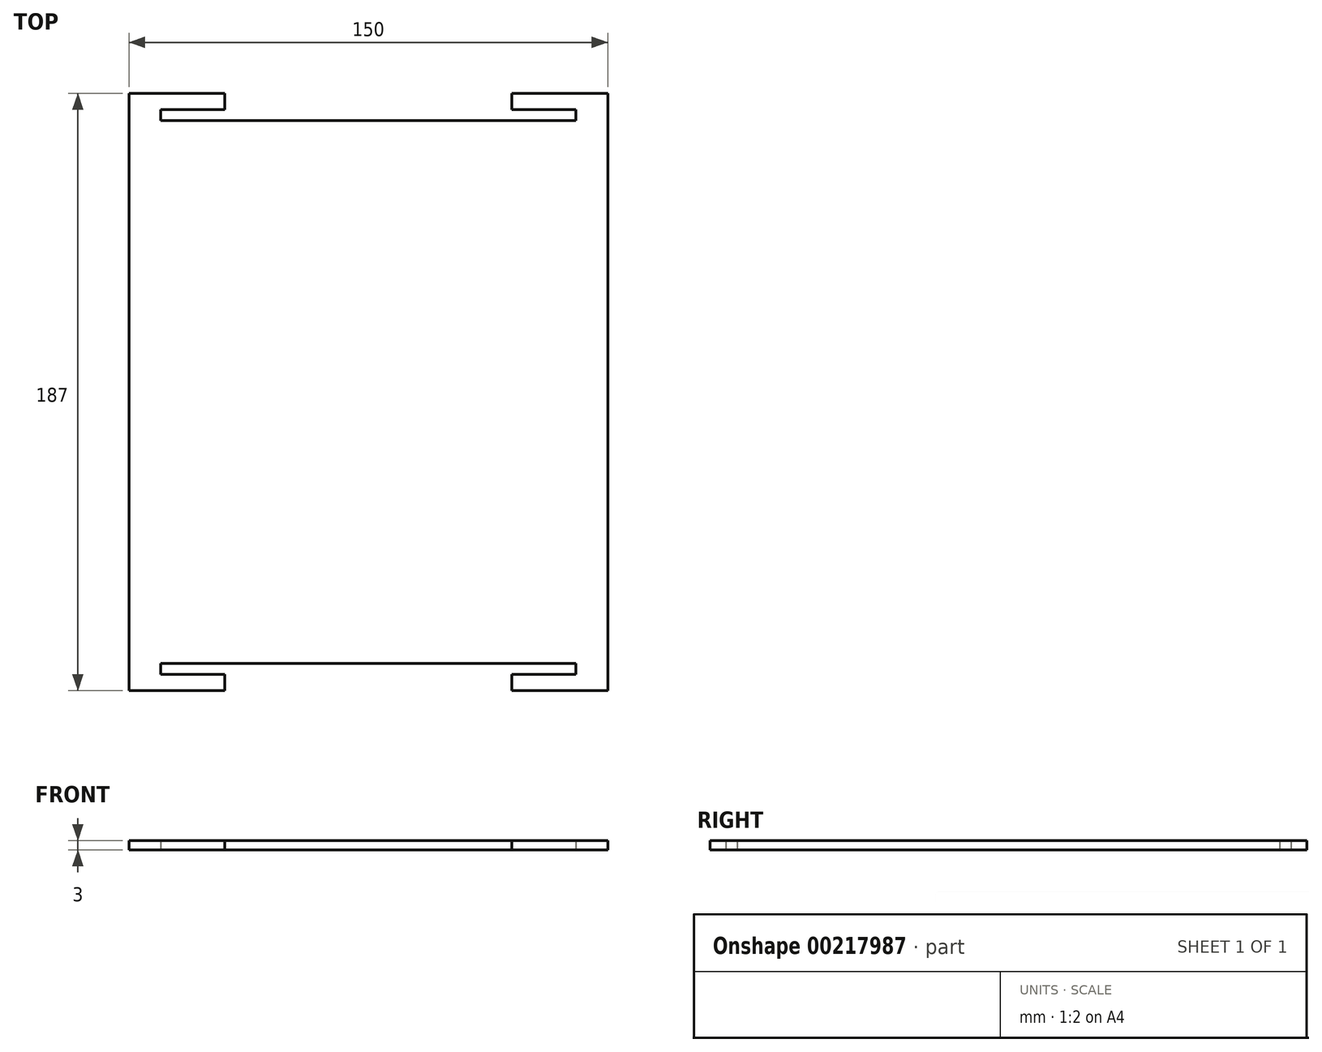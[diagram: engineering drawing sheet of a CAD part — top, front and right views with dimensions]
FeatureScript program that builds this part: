
annotation { "Feature Type Name" : "Feature", "Feature Type Description" : "" }
export const myFeature = defineFeature(function(context is Context, id is Id, definition is map)
    precondition{}
    {
        {
            var Q0;
            Q0=qCreatedBy(makeId("Top.planeOp"),FACE);
            var sketch = newSketch(context, id + "F0", { "sketchPlane" : qUnion([Q0])});
            skLineSegment(sketch, "E0.bottom", {"start": v(-37.91, 140.8) * mm, "end": v(112.09, 140.8) * mm});
            skLineSegment(sketch, "E0.top", {"start": v(-37.91, -29.2) * mm, "end": v(112.09, -29.2) * mm});
            skLineSegment(sketch, "E0.left", {"start": v(-37.91, 140.8) * mm, "end": v(-37.91, -29.2) * mm});
            skLineSegment(sketch, "E0.right", {"start": v(112.09, 140.8) * mm, "end": v(112.09, -29.2) * mm});
            skLineSegment(sketch, "E1", {"start": v(112.09, -29.2) * mm, "end": v(112.09, -37.7) * mm});
            skLineSegment(sketch, "E2", {"start": v(112.09, -37.7) * mm, "end": v(82.09, -37.7) * mm});
            skLineSegment(sketch, "E3", {"start": v(82.09, -37.7) * mm, "end": v(82.09, -32.7) * mm});
            skLineSegment(sketch, "E4", {"start": v(82.09, -32.7) * mm, "end": v(102.09, -32.7) * mm});
            skLineSegment(sketch, "E5", {"start": v(102.09, -32.7) * mm, "end": v(102.09, -29.2) * mm});
            skLineSegment(sketch, "E6", {"start": v(30.03, -29.2) * mm, "end": v(35.03, -29.2) * mm});
            skLineSegment(sketch, "E7", {"start": v(35.03, -29.2) * mm, "end": v(30.03, -29.2) * mm});
            skLineSegment(sketch, "E8", {"start": v(30.03, -29.2) * mm, "end": v(102.09, -29.2) * mm});
            skLineSegment(sketch, "E9.bottom", {"start": v(-37.91, -29.2) * mm, "end": v(-10.8, -29.2) * mm});
            skLineSegment(sketch, "E9.top", {"start": v(-37.91, -37.7) * mm, "end": v(-7.91, -37.7) * mm});
            skLineSegment(sketch, "E9.left", {"start": v(-37.91, -29.2) * mm, "end": v(-37.91, -37.7) * mm});
            skLineSegment(sketch, "E10.bottom", {"start": v(-10.8, -29.2) * mm, "end": v(-27.91, -29.2) * mm});
            skLineSegment(sketch, "E10.top", {"start": v(-7.91, -32.7) * mm, "end": v(-27.91, -32.7) * mm});
            skLineSegment(sketch, "E10.right", {"start": v(-27.91, -29.2) * mm, "end": v(-27.91, -32.7) * mm});
            skLineSegment(sketch, "E11", {"start": v(-7.91, -32.7) * mm, "end": v(-7.91, -37.7) * mm});
            skLineSegment(sketch, "E12", {"start": v(-37.91, 149.3) * mm, "end": v(-7.91, 149.3) * mm});
            skLineSegment(sketch, "E13", {"start": v(-7.91, 149.3) * mm, "end": v(-7.91, 144.3) * mm});
            skLineSegment(sketch, "E14", {"start": v(-7.91, 144.3) * mm, "end": v(-27.91, 144.3) * mm});
            skLineSegment(sketch, "E15", {"start": v(-27.91, 144.3) * mm, "end": v(-27.91, 140.8) * mm});
            skLineSegment(sketch, "E16", {"start": v(-27.91, 140.8) * mm, "end": v(112.09, 140.8) * mm});
            skLineSegment(sketch, "E17", {"start": v(112.09, 149.3) * mm, "end": v(82.09, 149.3) * mm});
            skLineSegment(sketch, "E18", {"start": v(82.09, 149.3) * mm, "end": v(82.09, 144.3) * mm});
            skLineSegment(sketch, "E19", {"start": v(82.09, 144.3) * mm, "end": v(102.09, 144.3) * mm});
            skLineSegment(sketch, "E20", {"start": v(102.09, 144.3) * mm, "end": v(102.09, 140.8) * mm});
            skLineSegment(sketch, "E21", {"start": v(112.09, 149.3) * mm, "end": v(112.09, 140.8) * mm});
            skLineSegment(sketch, "E22", {"start": v(112.09, 140.8) * mm, "end": v(112.09, 15.99) * mm});
            skLineSegment(sketch, "E23", {"start": v(-37.91, 149.3) * mm, "end": v(-37.91, 140.8) * mm});
            skSolve(sketch);
        }
        {
            var Q0;
            Q0 = qSketchRegion(id + "F0", true);
            extrude(context, id + "F1", {"entities" : qUnion([Q0]), "depth" : 3 * mm});
        }
    });
